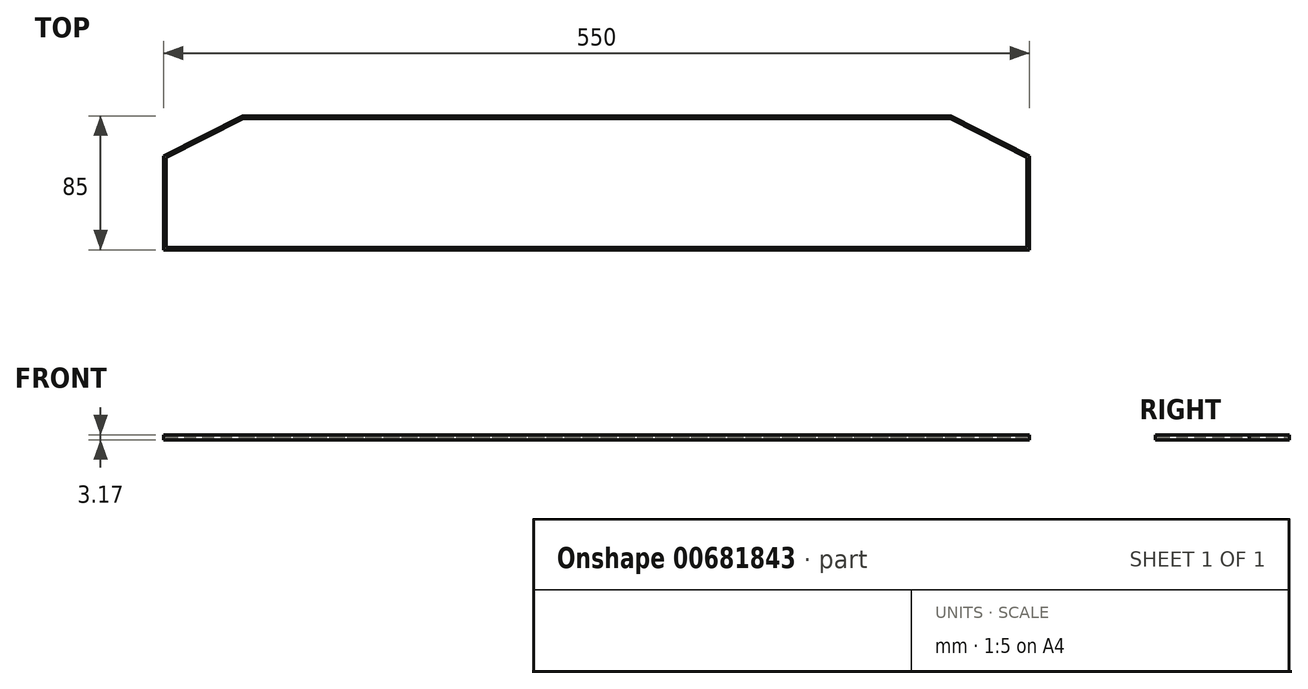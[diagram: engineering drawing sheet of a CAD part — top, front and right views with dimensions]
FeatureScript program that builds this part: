
annotation { "Feature Type Name" : "Feature", "Feature Type Description" : "" }
export const myFeature = defineFeature(function(context is Context, id is Id, definition is map)
    precondition{}
    {
        {
            var Q0;
            Q0=qCreatedBy(makeId("Top.planeOp"),FACE);
            var sketch = newSketch(context, id + "F0", { "sketchPlane" : qUnion([Q0])});
            skLineSegment(sketch, "E0.bottom", {"start": v(0, 0) * mm, "end": v(550, 0) * mm});
            skLineSegment(sketch, "E0.top", {"start": v(0, 85) * mm, "end": v(550, 85) * mm});
            skLineSegment(sketch, "E0.left", {"start": v(0, 0) * mm, "end": v(0, 85) * mm});
            skLineSegment(sketch, "E0.right", {"start": v(550, 0) * mm, "end": v(550, 85) * mm});
            skLineSegment(sketch, "E1", {"start": v(0, 59.6) * mm, "end": v(50, 85) * mm});
            skLineSegment(sketch, "E2", {"start": v(550, 59.6) * mm, "end": v(500, 85) * mm});
            skSolve(sketch);
        }
        {
            var Q0;
            {var subQ1=sQuery(id+"F0.wireOp",EDGE,"E0.bottom");Q0=makeQuery(id+"F0.imprint","IMPRINT",FACE,{"disambiguationData":[TD([[makeQuery(id+"F0.imprint","IMPRINT",EDGE,{"derivedFrom":subQ1}),1.0]])]});}
            extrude(context, id + "F1", {"entities" : qUnion([Q0]), "depth" : 3.17 * mm, "offsetDistance" : 25.4 * mm});
        }
        {
            var Q0;
            Q0=makeQuery(id+"F1.opExtrude","CAP_FACE",FACE,{"disambiguationData":[OSD([sQuery(id+"F0.wireOp",EDGE,"E0.bottom"),sQuery(id+"F0.wireOp",EDGE,"E0.top"),sQuery(id+"F0.wireOp",EDGE,"E0.left"),sQuery(id+"F0.wireOp",EDGE,"E0.right"),sQuery(id+"F0.wireOp",EDGE,"E1"),sQuery(id+"F0.wireOp",EDGE,"E2")])],"isStart":false});
            shell(context, id + "F2", {"entities" : qUnion([Q0]), "thickness" : 1.59 * mm});
        }
    });
